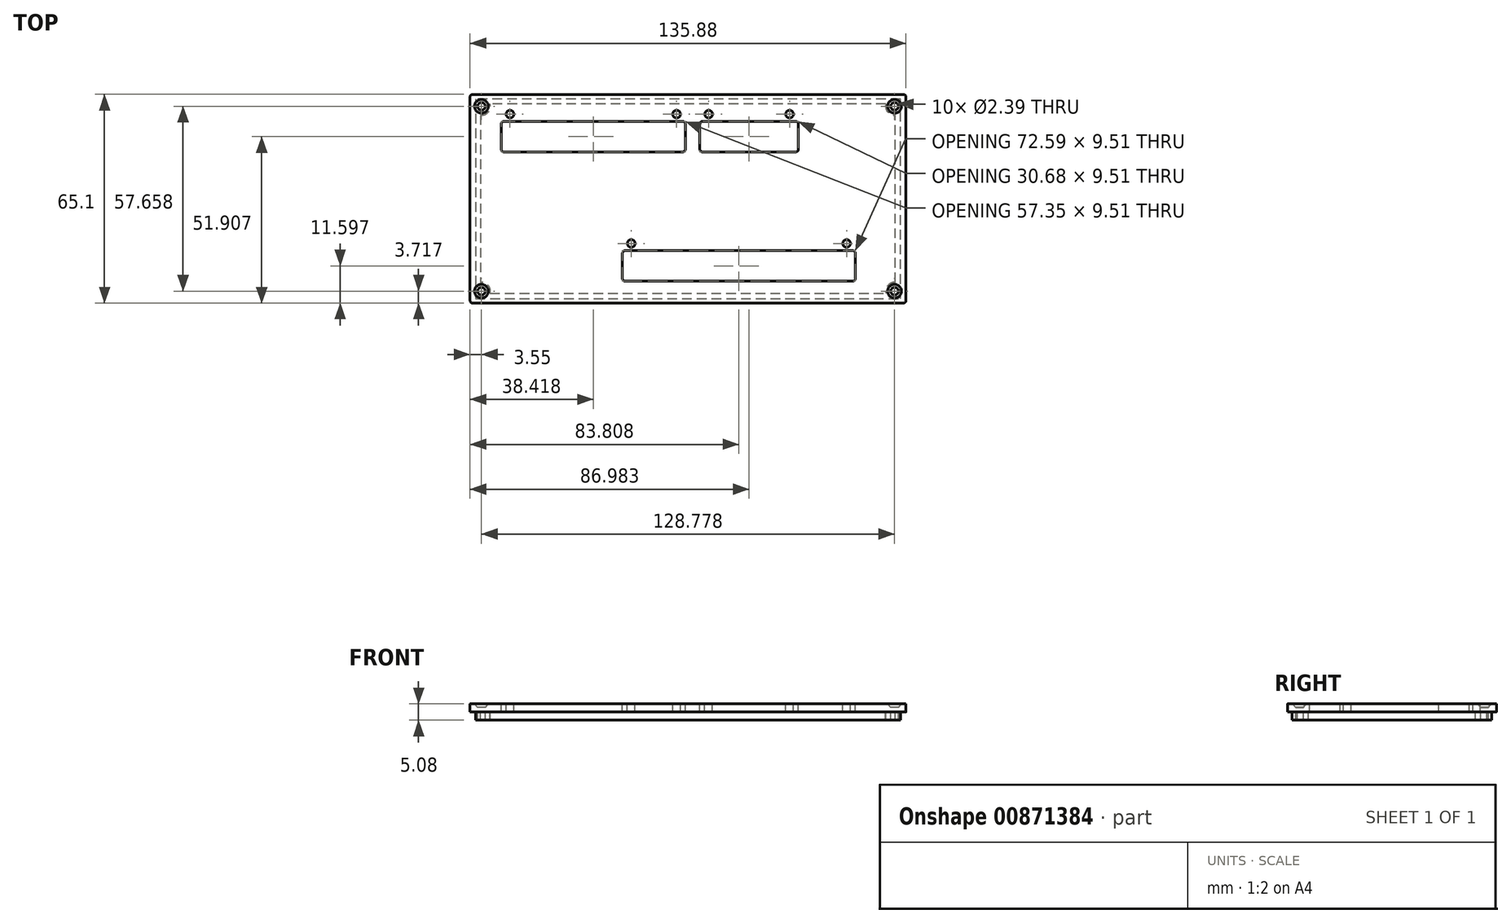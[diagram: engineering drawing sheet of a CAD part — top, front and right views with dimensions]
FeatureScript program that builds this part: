
annotation { "Feature Type Name" : "Feature", "Feature Type Description" : "" }
export const myFeature = defineFeature(function(context is Context, id is Id, definition is map)
    precondition{}
    {
        {
            var Q0;
            Q0=qCreatedBy(makeId("Top.planeOp"),FACE);
            var sketch = newSketch(context, id + "F0", { "sketchPlane" : qUnion([Q0])});
            skLineSegment(sketch, "E0.0", {"start": v(-833.13, 373.6) * mm, "end": v(-888.9, 373.6) * mm});
            skArc(sketch, "E0.1", {"start": v(-888.9, 373.6) * mm, "mid": v(-889.46, 373.37) * mm, "end": v(-889.69, 372.8) * mm});
            skLineSegment(sketch, "E0.2", {"start": v(-889.69, 372.8) * mm, "end": v(-889.69, 364.88) * mm});
            skArc(sketch, "E0.3", {"start": v(-889.69, 364.88) * mm, "mid": v(-889.46, 364.32) * mm, "end": v(-888.9, 364.1) * mm});
            skLineSegment(sketch, "E0.4", {"start": v(-888.9, 364.1) * mm, "end": v(-833.13, 364.1) * mm});
            skArc(sketch, "E0.5", {"start": v(-833.13, 364.1) * mm, "mid": v(-832.57, 364.32) * mm, "end": v(-832.34, 364.88) * mm});
            skLineSegment(sketch, "E0.6", {"start": v(-832.34, 364.88) * mm, "end": v(-832.34, 372.8) * mm});
            skArc(sketch, "E0.7", {"start": v(-832.34, 372.8) * mm, "mid": v(-832.57, 373.37) * mm, "end": v(-833.13, 373.6) * mm});
            skCircle(sketch, "E0.8", {"center": v(-886.97, 375.86) * mm, "radius": 1.2 * mm});
            skCircle(sketch, "E0.9", {"center": v(-835.05, 375.86) * mm, "radius": 1.2 * mm});
            skCircle(sketch, "E0.10", {"center": v(-825.07, 375.86) * mm, "radius": 1.2 * mm});
            skLineSegment(sketch, "E0.11", {"start": v(-797.9, 373.6) * mm, "end": v(-827, 373.6) * mm});
            skArc(sketch, "E0.12", {"start": v(-827, 373.6) * mm, "mid": v(-827.56, 373.37) * mm, "end": v(-827.79, 372.8) * mm});
            skLineSegment(sketch, "E0.13", {"start": v(-827.79, 372.8) * mm, "end": v(-827.79, 364.88) * mm});
            skArc(sketch, "E0.14", {"start": v(-827.79, 364.88) * mm, "mid": v(-827.56, 364.32) * mm, "end": v(-827, 364.1) * mm});
            skLineSegment(sketch, "E0.15", {"start": v(-827, 364.1) * mm, "end": v(-797.9, 364.1) * mm});
            skArc(sketch, "E0.16", {"start": v(-797.9, 364.1) * mm, "mid": v(-797.34, 364.32) * mm, "end": v(-797.1, 364.88) * mm});
            skLineSegment(sketch, "E0.17", {"start": v(-797.1, 364.88) * mm, "end": v(-797.1, 372.8) * mm});
            skArc(sketch, "E0.18", {"start": v(-797.1, 372.8) * mm, "mid": v(-797.34, 373.37) * mm, "end": v(-797.9, 373.6) * mm});
            skCircle(sketch, "E0.19", {"center": v(-799.82, 375.86) * mm, "radius": 1.2 * mm});
            skCircle(sketch, "E0.20", {"center": v(-782.04, 335.53) * mm, "radius": 1.2 * mm});
            skArc(sketch, "E0.21", {"start": v(-779.33, 332.5) * mm, "mid": v(-779.56, 333.06) * mm, "end": v(-780.12, 333.3) * mm});
            skLineSegment(sketch, "E0.22", {"start": v(-779.33, 324.57) * mm, "end": v(-779.33, 332.5) * mm});
            skLineSegment(sketch, "E0.23", {"start": v(-780.12, 333.3) * mm, "end": v(-851.12, 333.3) * mm});
            skArc(sketch, "E0.24", {"start": v(-780.12, 323.78) * mm, "mid": v(-779.56, 324.01) * mm, "end": v(-779.33, 324.57) * mm});
            skLineSegment(sketch, "E0.25", {"start": v(-851.12, 323.78) * mm, "end": v(-780.12, 323.78) * mm});
            skCircle(sketch, "E0.26", {"center": v(-849.2, 335.53) * mm, "radius": 1.2 * mm});
            skArc(sketch, "E0.27", {"start": v(-851.12, 333.3) * mm, "mid": v(-851.69, 333.06) * mm, "end": v(-851.92, 332.5) * mm});
            skLineSegment(sketch, "E0.28", {"start": v(-851.92, 332.5) * mm, "end": v(-851.92, 324.57) * mm});
            skArc(sketch, "E0.29", {"start": v(-851.92, 324.57) * mm, "mid": v(-851.69, 324.01) * mm, "end": v(-851.12, 323.78) * mm});
            skLineSegment(sketch, "E1.2", {"start": v(-764.35, 382.04) * mm, "end": v(-898.64, 382.04) * mm});
            skLineSegment(sketch, "E1.6", {"start": v(-898.64, 316.94) * mm, "end": v(-764.35, 316.94) * mm});
            skLineSegment(sketch, "E2.0", {"start": v(-899.43, 381.24) * mm, "end": v(-899.43, 317.73) * mm});
            skLineSegment(sketch, "E3.0", {"start": v(-763.55, 317.73) * mm, "end": v(-763.55, 381.24) * mm});
            skPoint(sketch, "E4.visualSharp", {"position": v(-899.43, 382.04) * mm});
            skArc(sketch, "E4.filletArc", {"start": v(-898.64, 382.04) * mm, "mid": v(-899.2, 381.8) * mm, "end": v(-899.43, 381.24) * mm});
            skPoint(sketch, "E5.visualSharp", {"position": v(-763.55, 382.04) * mm});
            skArc(sketch, "E5.filletArc", {"start": v(-763.55, 381.24) * mm, "mid": v(-763.78, 381.8) * mm, "end": v(-764.35, 382.04) * mm});
            skPoint(sketch, "E6.visualSharp", {"position": v(-763.55, 316.94) * mm});
            skArc(sketch, "E6.filletArc", {"start": v(-764.35, 316.94) * mm, "mid": v(-763.78, 317.17) * mm, "end": v(-763.55, 317.73) * mm});
            skPoint(sketch, "E7.visualSharp", {"position": v(-899.43, 316.94) * mm});
            skArc(sketch, "E7.filletArc", {"start": v(-899.43, 317.73) * mm, "mid": v(-899.2, 317.17) * mm, "end": v(-898.64, 316.94) * mm});
            skLineSegment(sketch, "E8", {"start": v(-831.5, 382.04) * mm, "end": v(-831.5, 316.94) * mm, "construction": true});
            skLineSegment(sketch, "E9.0", {"start": v(-895.88, 378.31) * mm, "end": v(-895.88, 320.66) * mm, "construction": true});
            skLineSegment(sketch, "E10.0", {"start": v(-767.1, 378.31) * mm, "end": v(-767.1, 320.66) * mm, "construction": true});
            skLineSegment(sketch, "E11", {"start": v(-899.43, 349.49) * mm, "end": v(-763.55, 349.49) * mm, "construction": true});
            skLineSegment(sketch, "E12.0", {"start": v(-895.88, 320.66) * mm, "end": v(-767.1, 320.66) * mm, "construction": true});
            skLineSegment(sketch, "E13.0", {"start": v(-895.88, 378.31) * mm, "end": v(-767.1, 378.31) * mm, "construction": true});
            skCircle(sketch, "E14", {"center": v(-895.88, 378.31) * mm, "radius": 1.2 * mm, "construction": true});
            skCircle(sketch, "E15", {"center": v(-767.1, 378.31) * mm, "radius": 1.2 * mm, "construction": true});
            skCircle(sketch, "E16", {"center": v(-767.1, 320.66) * mm, "radius": 1.2 * mm, "construction": true});
            skCircle(sketch, "E17", {"center": v(-895.88, 320.66) * mm, "radius": 1.2 * mm, "construction": true});
            skSolve(sketch);
        }
        {
            var Q0;
            Q0 = qSketchRegion(id + "F0", true);
            extrude(context, id + "F1", {"entities" : qUnion([Q0]), "oppositeDirection" : true, "depth" : 2.54 * mm, "offsetDistance" : 25.4 * mm});
        }
        {
            var Q0;
            Q0=makeQuery(id+"F1.opExtrude","CAP_FACE",FACE,{"disambiguationData":[OSD([sQuery(id+"F0.wireOp",EDGE,"E0.0"),sQuery(id+"F0.wireOp",EDGE,"E0.1"),sQuery(id+"F0.wireOp",EDGE,"E0.2"),sQuery(id+"F0.wireOp",EDGE,"E0.3"),sQuery(id+"F0.wireOp",EDGE,"E0.4"),sQuery(id+"F0.wireOp",EDGE,"E0.5"),sQuery(id+"F0.wireOp",EDGE,"E0.6"),sQuery(id+"F0.wireOp",EDGE,"E0.7"),sQuery(id+"F0.wireOp",EDGE,"E0.8"),sQuery(id+"F0.wireOp",EDGE,"E0.9"),sQuery(id+"F0.wireOp",EDGE,"E0.10"),sQuery(id+"F0.wireOp",EDGE,"E0.11"),sQuery(id+"F0.wireOp",EDGE,"E0.12"),sQuery(id+"F0.wireOp",EDGE,"E0.13"),sQuery(id+"F0.wireOp",EDGE,"E0.14"),sQuery(id+"F0.wireOp",EDGE,"E0.15"),sQuery(id+"F0.wireOp",EDGE,"E0.16"),sQuery(id+"F0.wireOp",EDGE,"E0.17"),sQuery(id+"F0.wireOp",EDGE,"E0.18"),sQuery(id+"F0.wireOp",EDGE,"E0.19"),sQuery(id+"F0.wireOp",EDGE,"E0.20"),sQuery(id+"F0.wireOp",EDGE,"E0.21"),sQuery(id+"F0.wireOp",EDGE,"E0.22"),sQuery(id+"F0.wireOp",EDGE,"E0.23"),sQuery(id+"F0.wireOp",EDGE,"E0.24"),sQuery(id+"F0.wireOp",EDGE,"E0.25"),sQuery(id+"F0.wireOp",EDGE,"E0.26"),sQuery(id+"F0.wireOp",EDGE,"E0.27"),sQuery(id+"F0.wireOp",EDGE,"E0.28"),sQuery(id+"F0.wireOp",EDGE,"E0.29"),sQuery(id+"F0.wireOp",EDGE,"E1.2"),sQuery(id+"F0.wireOp",EDGE,"E1.6"),sQuery(id+"F0.wireOp",EDGE,"E2.0"),sQuery(id+"F0.wireOp",EDGE,"E3.0"),sQuery(id+"F0.wireOp",EDGE,"E4.filletArc"),sQuery(id+"F0.wireOp",EDGE,"E5.filletArc"),sQuery(id+"F0.wireOp",EDGE,"E6.filletArc"),sQuery(id+"F0.wireOp",EDGE,"E7.filletArc")])],"isStart":false});
            var sketch = newSketch(context, id + "F2", { "sketchPlane" : qUnion([Q0])});
            skLineSegment(sketch, "E18.0", {"start": v(-765.25, -318.37) * mm, "end": v(-765.25, -380.6) * mm});
            skLineSegment(sketch, "E19.0", {"start": v(-897.73, -380.6) * mm, "end": v(-897.73, -318.37) * mm});
            skLineSegment(sketch, "E20.0", {"start": v(-765.25, -380.6) * mm, "end": v(-897.73, -380.6) * mm});
            skLineSegment(sketch, "E21.0", {"start": v(-897.73, -318.37) * mm, "end": v(-765.25, -318.37) * mm});
            skLineSegment(sketch, "E22.1", {"start": v(-766.84, -323.43) * mm, "end": v(-766.84, -375.55) * mm});
            skLineSegment(sketch, "E22.3", {"start": v(-896.14, -375.55) * mm, "end": v(-896.14, -323.43) * mm});
            skArc(sketch, "E23.0", {"start": v(-896.14, -323.43) * mm, "mid": v(-893.76, -322.46) * mm, "end": v(-893.19, -319.96) * mm});
            skArc(sketch, "E24.0", {"start": v(-769.8, -319.96) * mm, "mid": v(-769.22, -322.46) * mm, "end": v(-766.84, -323.43) * mm});
            skLineSegment(sketch, "E25.trimOffspring", {"start": v(-769.8, -379.01) * mm, "end": v(-893.19, -379.01) * mm});
            skArc(sketch, "E26.trimOffspring", {"start": v(-766.84, -375.55) * mm, "mid": v(-769.22, -376.51) * mm, "end": v(-769.8, -379.01) * mm});
            skArc(sketch, "E27.trimOffspring", {"start": v(-893.19, -379.01) * mm, "mid": v(-893.76, -376.51) * mm, "end": v(-896.14, -375.55) * mm});
            skLineSegment(sketch, "E28.trimOffspring", {"start": v(-893.19, -319.96) * mm, "end": v(-769.8, -319.96) * mm});
            skSolve(sketch);
        }
        {
            var Q0;
            Q0 = qSketchRegion(id + "F2", true);
            extrude(context, id + "F3", {"entities" : qUnion([Q0]), "operationType" : NewBodyOperationType.ADD, "depth" : 2.54 * mm, "offsetDistance" : 25.4 * mm});
        }
        {
            var Q0;
            Q0=sQuery(id+"F0.wireOp",VERTEX,"E9.0.start");
            var Q1;
            Q1=sQuery(id+"F0.wireOp",VERTEX,"E10.0.start");
            var Q2;
            Q2=sQuery(id+"F0.wireOp",VERTEX,"E10.0.end");
            var Q3;
            Q3=sQuery(id+"F0.wireOp",VERTEX,"E9.0.end");
            var Q4;
            Q4=makeQuery(id+"F1.opExtrude","SWEPT_BODY",BODY,{"disambiguationData":[OSD([sQuery(id+"F0.wireOp",EDGE,"E0.0"),sQuery(id+"F0.wireOp",EDGE,"E0.1"),sQuery(id+"F0.wireOp",EDGE,"E0.2"),sQuery(id+"F0.wireOp",EDGE,"E0.3"),sQuery(id+"F0.wireOp",EDGE,"E0.4"),sQuery(id+"F0.wireOp",EDGE,"E0.5"),sQuery(id+"F0.wireOp",EDGE,"E0.6"),sQuery(id+"F0.wireOp",EDGE,"E0.7"),sQuery(id+"F0.wireOp",EDGE,"E0.8"),sQuery(id+"F0.wireOp",EDGE,"E0.9"),sQuery(id+"F0.wireOp",EDGE,"E0.10"),sQuery(id+"F0.wireOp",EDGE,"E0.11"),sQuery(id+"F0.wireOp",EDGE,"E0.12"),sQuery(id+"F0.wireOp",EDGE,"E0.13"),sQuery(id+"F0.wireOp",EDGE,"E0.14"),sQuery(id+"F0.wireOp",EDGE,"E0.15"),sQuery(id+"F0.wireOp",EDGE,"E0.16"),sQuery(id+"F0.wireOp",EDGE,"E0.17"),sQuery(id+"F0.wireOp",EDGE,"E0.18"),sQuery(id+"F0.wireOp",EDGE,"E0.19"),sQuery(id+"F0.wireOp",EDGE,"E0.20"),sQuery(id+"F0.wireOp",EDGE,"E0.21"),sQuery(id+"F0.wireOp",EDGE,"E0.22"),sQuery(id+"F0.wireOp",EDGE,"E0.23"),sQuery(id+"F0.wireOp",EDGE,"E0.24"),sQuery(id+"F0.wireOp",EDGE,"E0.25"),sQuery(id+"F0.wireOp",EDGE,"E0.26"),sQuery(id+"F0.wireOp",EDGE,"E0.27"),sQuery(id+"F0.wireOp",EDGE,"E0.28"),sQuery(id+"F0.wireOp",EDGE,"E0.29"),sQuery(id+"F0.wireOp",EDGE,"E1.2"),sQuery(id+"F0.wireOp",EDGE,"E1.6"),sQuery(id+"F0.wireOp",EDGE,"E2.0"),sQuery(id+"F0.wireOp",EDGE,"E3.0"),sQuery(id+"F0.wireOp",EDGE,"E4.filletArc"),sQuery(id+"F0.wireOp",EDGE,"E5.filletArc"),sQuery(id+"F0.wireOp",EDGE,"E6.filletArc"),sQuery(id+"F0.wireOp",EDGE,"E7.filletArc")])]});
            hole(context, id + "F4", {"style" : HoleStyle.C_SINK, "endStyle" : HoleEndStyle.THROUGH, "holeDiameter" : 2.4 * mm, "cSinkDiameter" : 4.32 * mm, "cSinkAngle" : 82 * degree, "majorDiameter" : 6.35 * mm, "isTappedThrough" : true, "tappedDepth" : 12.7 * mm, "tapClearance" : 3, "locations" : qUnion([Q0, Q1, Q2, Q3]), "scope" : qUnion([Q4])});
        }
    });
